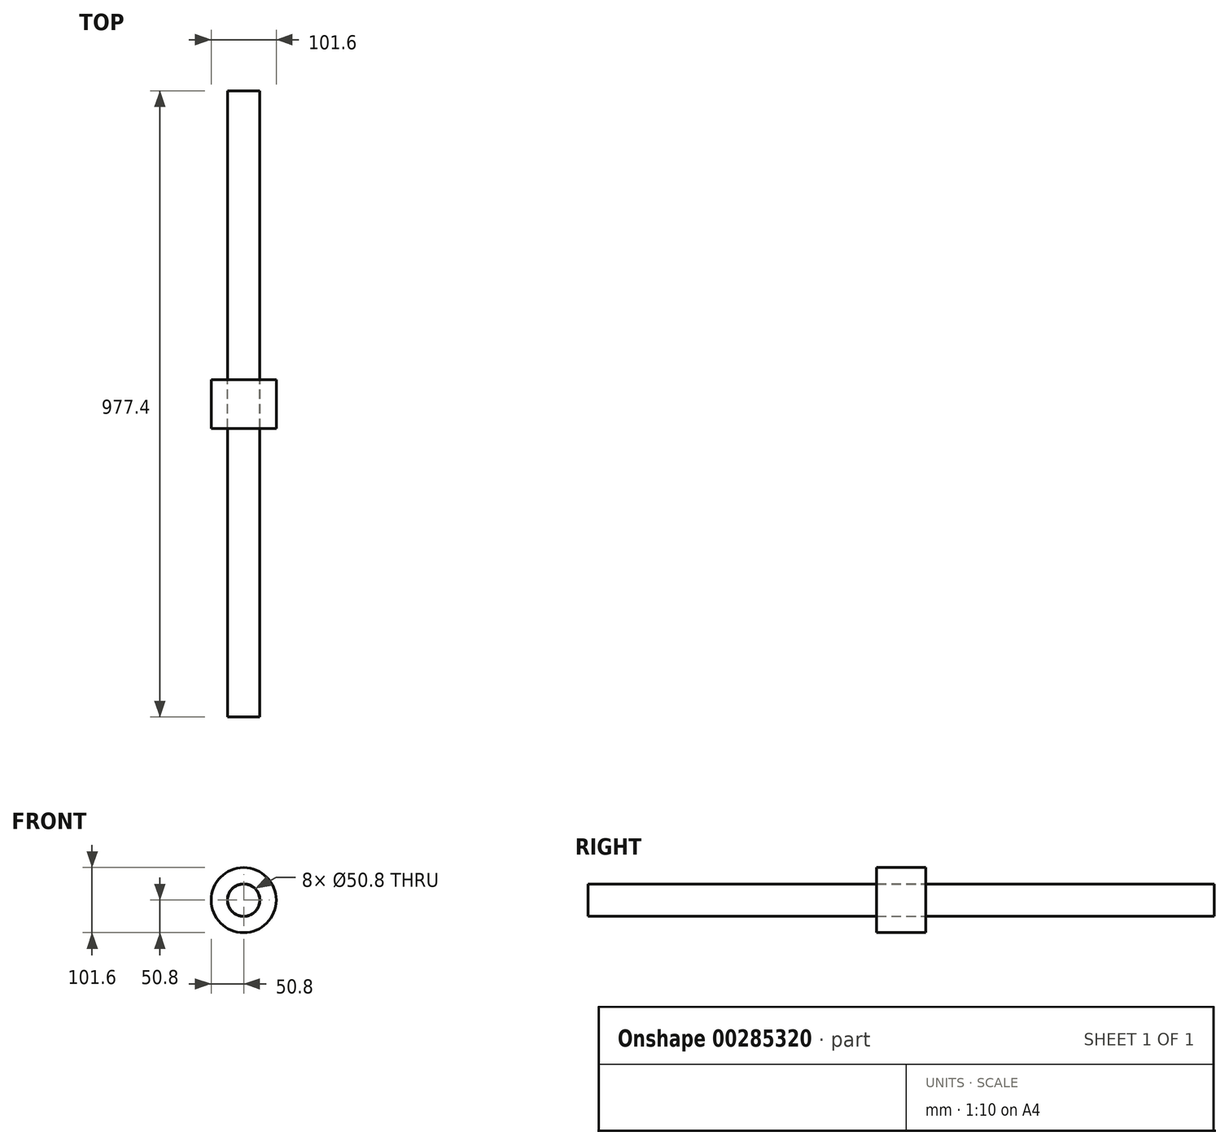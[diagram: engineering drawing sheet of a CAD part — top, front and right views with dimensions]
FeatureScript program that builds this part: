
annotation { "Feature Type Name" : "Feature", "Feature Type Description" : "" }
export const myFeature = defineFeature(function(context is Context, id is Id, definition is map)
    precondition{}
    {
        {
            var Q0;
            Q0=qCreatedBy(makeId("Front.planeOp"),FACE);
            var sketch = newSketch(context, id + "F0", { "sketchPlane" : qUnion([Q0])});
            skCircle(sketch, "E0", {"center": v(0, 0) * mm, "radius": 25.15 * mm});
            skSolve(sketch);
        }
        {
            var Q0;
            Q0=qCreatedBy(makeId("Front.planeOp"),FACE);
            var sketch = newSketch(context, id + "F1", { "sketchPlane" : qUnion([Q0])});
            skCircle(sketch, "E1", {"center": v(0, 0) * mm, "radius": 50.8 * mm});
            skCircle(sketch, "E2", {"center": v(0, 0) * mm, "radius": 25.4 * mm});
            skSolve(sketch);
        }
        {
            var Q0;
            Q0=makeQuery(id+"F1.imprint","IMPRINT",FACE,{"disambiguationData":[TD([[makeQuery(id+"F1.imprint","IMPRINT",EDGE,{"derivedFrom":sQuery(id+"F1.wireOp",EDGE,"E1")}),1.0]])]});
            extrude(context, id + "F2", {"entities" : qUnion([Q0]), "endBound" : BoundingType.SYMMETRIC, "depth" : 76.2 * mm});
        }
        {
            var Q0;
            Q0=makeQuery(id+"F0.imprint","IMPRINT",FACE,{"disambiguationData":[TD([[makeQuery(id+"F0.imprint","IMPRINT",EDGE,{"derivedFrom":sQuery(id+"F0.wireOp",EDGE,"E0")}),1.0]])]});
            var Q1;
            Q1=sQuery(id+"F0.wireOp",EDGE,"E0");
            extrude(context, id + "F3", {"entities" : qUnion([Q0]), "surfaceEntities" : qUnion([Q1]), "endBound" : BoundingType.SYMMETRIC, "depth" : 977.4 * mm});
        }
    });
